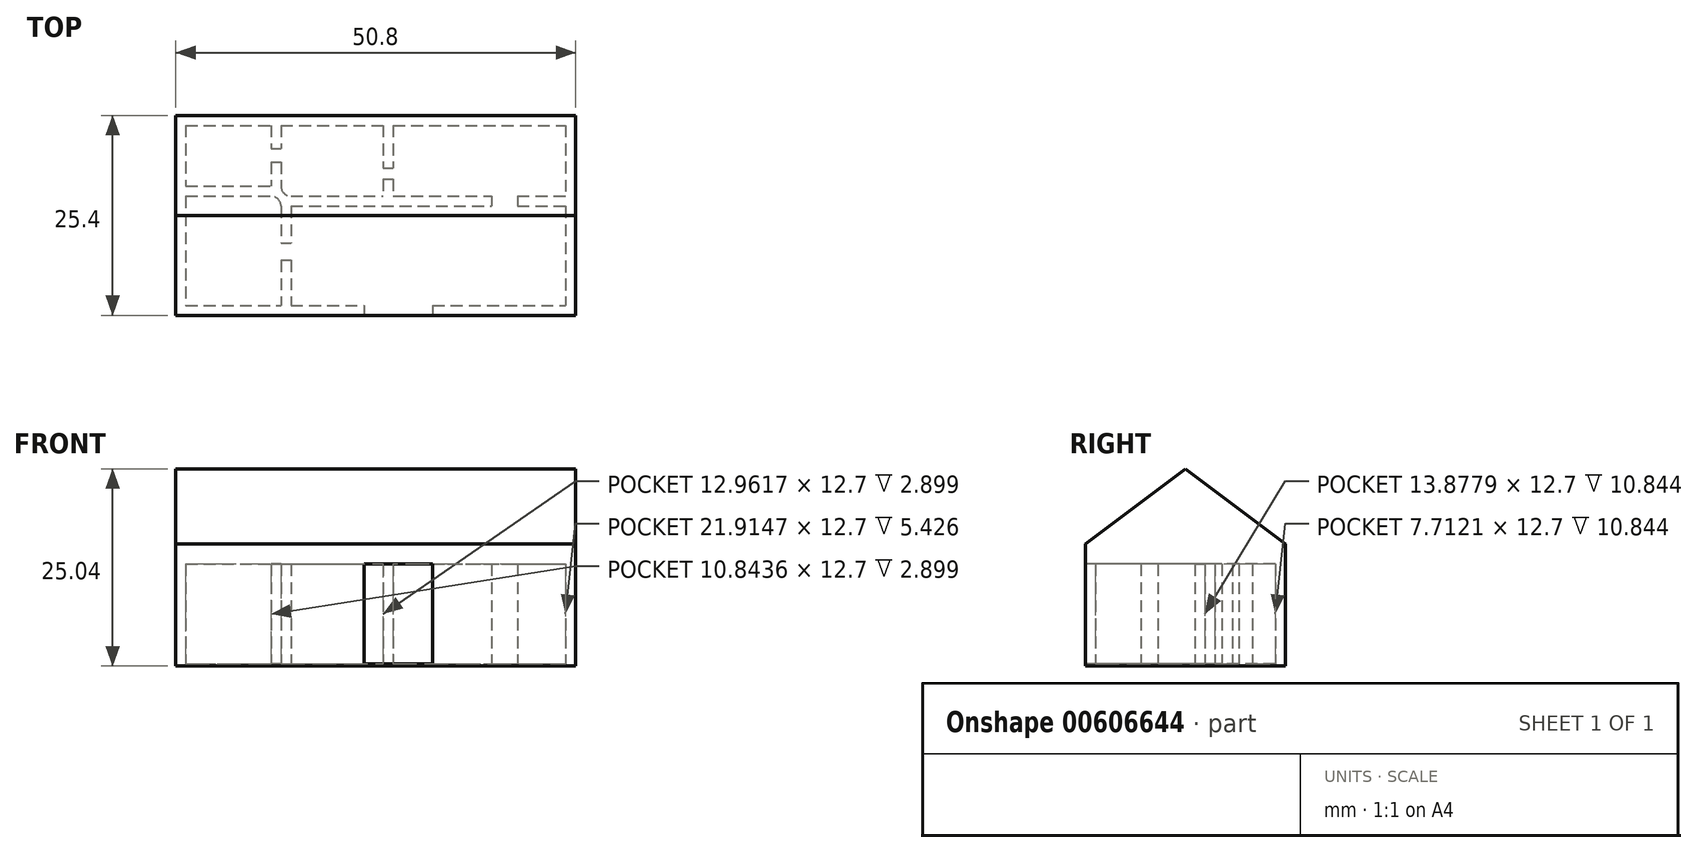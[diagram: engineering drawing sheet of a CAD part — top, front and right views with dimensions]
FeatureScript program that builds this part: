
annotation { "Feature Type Name" : "Feature", "Feature Type Description" : "" }
export const myFeature = defineFeature(function(context is Context, id is Id, definition is map)
    precondition{}
    {
        {
            var Q0;
            Q0=qCreatedBy(makeId("Top.planeOp"),FACE);
            var sketch = newSketch(context, id + "F0", { "sketchPlane" : qUnion([Q0])});
            skLineSegment(sketch, "E0.bottom", {"start": v(-23.3, 5.4) * mm, "end": v(27.5, 5.4) * mm});
            skLineSegment(sketch, "E0.top", {"start": v(-23.3, -20) * mm, "end": v(0.6, -20) * mm});
            skLineSegment(sketch, "E0.left", {"start": v(-23.3, 5.4) * mm, "end": v(-23.3, -20) * mm});
            skLineSegment(sketch, "E0.right", {"start": v(27.5, 5.4) * mm, "end": v(27.5, -20) * mm});
            skLineSegment(sketch, "E1.0", {"start": v(-22.03, 4.13) * mm, "end": v(3.04, 4.13) * mm});
            skLineSegment(sketch, "E1.1", {"start": v(-22.03, 4.13) * mm, "end": v(-22.03, -18.73) * mm});
            skLineSegment(sketch, "E1.2", {"start": v(-22.03, -18.73) * mm, "end": v(0.6, -18.73) * mm});
            skLineSegment(sketch, "E1.3", {"start": v(26.23, 4.13) * mm, "end": v(26.23, -18.73) * mm});
            skLineSegment(sketch, "E2", {"start": v(0.6, -18.73) * mm, "end": v(0.6, -20) * mm});
            skLineSegment(sketch, "E3", {"start": v(9.35, -18.73) * mm, "end": v(9.35, -20) * mm});
            skLineSegment(sketch, "E4.trimOffspring", {"start": v(9.35, -18.73) * mm, "end": v(26.23, -18.73) * mm});
            skLineSegment(sketch, "E5.trimOffspring", {"start": v(9.35, -20) * mm, "end": v(27.5, -20) * mm});
            skLineSegment(sketch, "E6.bottom", {"start": v(-22.03, 4.13) * mm, "end": v(-9.92, 4.13) * mm});
            skLineSegment(sketch, "E6.top", {"start": v(-22.03, -4.85) * mm, "end": v(-11.2, -4.85) * mm});
            skLineSegment(sketch, "E6.left", {"start": v(-22.03, 4.13) * mm, "end": v(-22.03, -4.85) * mm});
            skLineSegment(sketch, "E6.right", {"start": v(-9.92, 4.13) * mm, "end": v(-9.92, 1.23) * mm});
            skLineSegment(sketch, "E7.bottom", {"start": v(-8.65, -4.85) * mm, "end": v(3.04, -4.85) * mm});
            skLineSegment(sketch, "E7.top", {"start": v(-9.92, -18.73) * mm, "end": v(0.6, -18.73) * mm});
            skLineSegment(sketch, "E7.left", {"start": v(-9.92, -6.12) * mm, "end": v(-9.92, -10.78) * mm});
            skLineSegment(sketch, "E7.right", {"start": v(26.23, -4.85) * mm, "end": v(26.23, -18.73) * mm});
            skLineSegment(sketch, "E8.0", {"start": v(-22.03, -3.58) * mm, "end": v(-11.2, -3.58) * mm});
            skLineSegment(sketch, "E8.1", {"start": v(-11.2, 4.13) * mm, "end": v(-11.2, 1.23) * mm});
            skLineSegment(sketch, "E9.0", {"start": v(-8.65, -6.12) * mm, "end": v(16.82, -6.12) * mm});
            skLineSegment(sketch, "E9.1", {"start": v(-8.65, -6.12) * mm, "end": v(-8.65, -10.78) * mm});
            skArc(sketch, "E10", {"start": v(-9.92, -6.12) * mm, "mid": v(-10.3, -5.23) * mm, "end": v(-11.2, -4.85) * mm});
            skArc(sketch, "E11", {"start": v(-9.92, -3.58) * mm, "mid": v(-9.55, -4.48) * mm, "end": v(-8.65, -4.85) * mm});
            skLineSegment(sketch, "E12", {"start": v(-11.2, 1.23) * mm, "end": v(-9.92, 1.23) * mm});
            skLineSegment(sketch, "E13", {"start": v(-11.2, -0.52) * mm, "end": v(-9.92, -0.52) * mm});
            skLineSegment(sketch, "E14", {"start": v(-9.92, -10.78) * mm, "end": v(-8.65, -10.78) * mm});
            skPoint(sketch, "E14.endSnap0", {"position": v(-8.65, -12.43) * mm});
            skLineSegment(sketch, "E15", {"start": v(-9.92, -12.98) * mm, "end": v(-8.65, -12.98) * mm});
            skLineSegment(sketch, "E16", {"start": v(16.82, -4.85) * mm, "end": v(16.82, -6.12) * mm});
            skLineSegment(sketch, "E17", {"start": v(20.12, -4.85) * mm, "end": v(20.12, -6.12) * mm});
            skLineSegment(sketch, "E18.trimOffspring", {"start": v(-11.2, -0.52) * mm, "end": v(-11.2, -3.58) * mm});
            skLineSegment(sketch, "E19.trimOffspring", {"start": v(-9.92, -0.52) * mm, "end": v(-9.92, -3.58) * mm});
            skLineSegment(sketch, "E20.trimOffspring", {"start": v(-9.92, -12.98) * mm, "end": v(-9.92, -18.73) * mm});
            skLineSegment(sketch, "E21.trimOffspring", {"start": v(-8.65, -12.43) * mm, "end": v(-8.65, -18.73) * mm});
            skLineSegment(sketch, "E22.trimOffspring", {"start": v(20.12, -6.12) * mm, "end": v(26.23, -6.12) * mm});
            skLineSegment(sketch, "E23.trimOffspring", {"start": v(20.12, -4.85) * mm, "end": v(26.23, -4.85) * mm});
            skLineSegment(sketch, "E24", {"start": v(4.31, 4.13) * mm, "end": v(4.31, -1.3) * mm});
            skLineSegment(sketch, "E25.0", {"start": v(3.04, 4.13) * mm, "end": v(3.04, -1.3) * mm});
            skLineSegment(sketch, "E26", {"start": v(3.04, -1.3) * mm, "end": v(4.31, -1.3) * mm});
            skLineSegment(sketch, "E27", {"start": v(3.04, -2.67) * mm, "end": v(4.31, -2.67) * mm});
            skLineSegment(sketch, "E28.trimOffspring", {"start": v(3.04, -2.67) * mm, "end": v(3.04, -4.85) * mm});
            skLineSegment(sketch, "E29.trimOffspring", {"start": v(4.31, -2.67) * mm, "end": v(4.31, -4.85) * mm});
            skLineSegment(sketch, "E30.trimOffspring", {"start": v(4.31, -4.85) * mm, "end": v(16.82, -4.85) * mm});
            skLineSegment(sketch, "E31.trimOffspring", {"start": v(4.31, 4.13) * mm, "end": v(26.23, 4.13) * mm});
            skSolve(sketch);
        }
        {
            var Q0;
            Q0 = qSketchRegion(id + "F0", true);
            extrude(context, id + "F1", {"entities" : qUnion([Q0]), "depth" : 12.7 * mm, "offsetDistance" : 25.4 * mm});
        }
        {
            var Q0;
            Q0=makeQuery(id+"F1.opExtrude","CAP_FACE",FACE,{"disambiguationData":[OSD([sQuery(id+"F0.wireOp",EDGE,"E0.bottom"),sQuery(id+"F0.wireOp",EDGE,"E0.top"),sQuery(id+"F0.wireOp",EDGE,"E0.left"),sQuery(id+"F0.wireOp",EDGE,"E0.right"),sQuery(id+"F0.wireOp",EDGE,"E1.0"),sQuery(id+"F0.wireOp",EDGE,"E1.1"),sQuery(id+"F0.wireOp",EDGE,"E1.2"),sQuery(id+"F0.wireOp",EDGE,"E1.3"),sQuery(id+"F0.wireOp",EDGE,"E2"),sQuery(id+"F0.wireOp",EDGE,"E3"),sQuery(id+"F0.wireOp",EDGE,"E5.trimOffspring"),sQuery(id+"F0.wireOp",EDGE,"E6.bottom"),sQuery(id+"F0.wireOp",EDGE,"E6.top"),sQuery(id+"F0.wireOp",EDGE,"E6.left"),sQuery(id+"F0.wireOp",EDGE,"E6.right"),sQuery(id+"F0.wireOp",EDGE,"E7.bottom"),sQuery(id+"F0.wireOp",EDGE,"E7.top"),sQuery(id+"F0.wireOp",EDGE,"E7.left"),sQuery(id+"F0.wireOp",EDGE,"E7.right"),sQuery(id+"F0.wireOp",EDGE,"E8.0"),sQuery(id+"F0.wireOp",EDGE,"E8.1"),sQuery(id+"F0.wireOp",EDGE,"E9.0"),sQuery(id+"F0.wireOp",EDGE,"E9.1"),sQuery(id+"F0.wireOp",EDGE,"E10"),sQuery(id+"F0.wireOp",EDGE,"E11"),sQuery(id+"F0.wireOp",EDGE,"E12"),sQuery(id+"F0.wireOp",EDGE,"E13"),sQuery(id+"F0.wireOp",EDGE,"E14"),sQuery(id+"F0.wireOp",EDGE,"E15"),sQuery(id+"F0.wireOp",EDGE,"E16"),sQuery(id+"F0.wireOp",EDGE,"E17"),sQuery(id+"F0.wireOp",EDGE,"E18.trimOffspring"),sQuery(id+"F0.wireOp",EDGE,"E19.trimOffspring"),sQuery(id+"F0.wireOp",EDGE,"E20.trimOffspring"),sQuery(id+"F0.wireOp",EDGE,"E21.trimOffspring"),sQuery(id+"F0.wireOp",EDGE,"E4.trimOffspring"),sQuery(id+"F0.wireOp",EDGE,"E22.trimOffspring"),sQuery(id+"F0.wireOp",EDGE,"E23.trimOffspring"),sQuery(id+"F0.wireOp",EDGE,"E24"),sQuery(id+"F0.wireOp",EDGE,"E25.0"),sQuery(id+"F0.wireOp",EDGE,"E26"),sQuery(id+"F0.wireOp",EDGE,"E27"),sQuery(id+"F0.wireOp",EDGE,"E28.trimOffspring"),sQuery(id+"F0.wireOp",EDGE,"E29.trimOffspring"),sQuery(id+"F0.wireOp",EDGE,"E30.trimOffspring"),sQuery(id+"F0.wireOp",EDGE,"E31.trimOffspring")])],"isStart":false});
            var sketch = newSketch(context, id + "F2", { "sketchPlane" : qUnion([Q0])});
            skLineSegment(sketch, "E32.bottom", {"start": v(-23.3, 5.4) * mm, "end": v(27.5, 5.4) * mm});
            skLineSegment(sketch, "E32.top", {"start": v(-23.3, -20) * mm, "end": v(27.5, -20) * mm});
            skLineSegment(sketch, "E32.left", {"start": v(-23.3, 5.4) * mm, "end": v(-23.3, -20) * mm});
            skLineSegment(sketch, "E32.right", {"start": v(27.5, 5.4) * mm, "end": v(27.5, -20) * mm});
            skSolve(sketch);
        }
        {
            var Q0;
            Q0 = qSketchRegion(id + "F2", true);
            extrude(context, id + "F3", {"entities" : qUnion([Q0]), "operationType" : NewBodyOperationType.ADD, "depth" : 2.54 * mm, "offsetDistance" : 25.4 * mm});
        }
        {
            var Q0;
            Q0=makeQuery(id+"F3.boolean.opBoolean","MERGE",FACE,{"derivedFrom":[makeQuery(id+"F1.opExtrude","SWEPT_FACE",FACE,{"disambiguationData":[OSD([sQuery(id+"F0.wireOp",EDGE,"E0.left")])]}),makeQuery(id+"F3.opExtrude","SWEPT_FACE",FACE,{"disambiguationData":[OSD([sQuery(id+"F2.wireOp",EDGE,"E32.left")])]})]});
            var sketch = newSketch(context, id + "F4", { "sketchPlane" : qUnion([Q0])});
            skLineSegment(sketch, "E33", {"start": v(-5.4, 15.24) * mm, "end": v(7.3, 24.79) * mm});
            skPoint(sketch, "E33.endSnap0", {"position": v(7.3, 15.24) * mm});
            skLineSegment(sketch, "E34", {"start": v(7.3, 24.79) * mm, "end": v(20, 15.24) * mm});
            skLineSegment(sketch, "E35", {"start": v(-5.4, 15.24) * mm, "end": v(20, 15.24) * mm});
            skSolve(sketch);
        }
        {
            var Q0;
            Q0 = qSketchRegion(id + "F4", true);
            extrude(context, id + "F5", {"entities" : qUnion([Q0]), "operationType" : NewBodyOperationType.ADD, "oppositeDirection" : true, "depth" : 50.8 * mm, "offsetDistance" : 25.4 * mm});
        }
        {
            var Q0;
            Q0=makeQuery(id+"F1.opExtrude","CAP_FACE",FACE,{"disambiguationData":[OSD([sQuery(id+"F0.wireOp",EDGE,"E0.bottom"),sQuery(id+"F0.wireOp",EDGE,"E0.top"),sQuery(id+"F0.wireOp",EDGE,"E0.left"),sQuery(id+"F0.wireOp",EDGE,"E0.right"),sQuery(id+"F0.wireOp",EDGE,"E1.0"),sQuery(id+"F0.wireOp",EDGE,"E1.1"),sQuery(id+"F0.wireOp",EDGE,"E1.2"),sQuery(id+"F0.wireOp",EDGE,"E1.3"),sQuery(id+"F0.wireOp",EDGE,"E2"),sQuery(id+"F0.wireOp",EDGE,"E3"),sQuery(id+"F0.wireOp",EDGE,"E5.trimOffspring"),sQuery(id+"F0.wireOp",EDGE,"E6.bottom"),sQuery(id+"F0.wireOp",EDGE,"E6.top"),sQuery(id+"F0.wireOp",EDGE,"E6.left"),sQuery(id+"F0.wireOp",EDGE,"E6.right"),sQuery(id+"F0.wireOp",EDGE,"E7.bottom"),sQuery(id+"F0.wireOp",EDGE,"E7.top"),sQuery(id+"F0.wireOp",EDGE,"E7.left"),sQuery(id+"F0.wireOp",EDGE,"E7.right"),sQuery(id+"F0.wireOp",EDGE,"E8.0"),sQuery(id+"F0.wireOp",EDGE,"E8.1"),sQuery(id+"F0.wireOp",EDGE,"E9.0"),sQuery(id+"F0.wireOp",EDGE,"E9.1"),sQuery(id+"F0.wireOp",EDGE,"E10"),sQuery(id+"F0.wireOp",EDGE,"E11"),sQuery(id+"F0.wireOp",EDGE,"E12"),sQuery(id+"F0.wireOp",EDGE,"E13"),sQuery(id+"F0.wireOp",EDGE,"E14"),sQuery(id+"F0.wireOp",EDGE,"E15"),sQuery(id+"F0.wireOp",EDGE,"E16"),sQuery(id+"F0.wireOp",EDGE,"E17"),sQuery(id+"F0.wireOp",EDGE,"E18.trimOffspring"),sQuery(id+"F0.wireOp",EDGE,"E19.trimOffspring"),sQuery(id+"F0.wireOp",EDGE,"E20.trimOffspring"),sQuery(id+"F0.wireOp",EDGE,"E21.trimOffspring"),sQuery(id+"F0.wireOp",EDGE,"E4.trimOffspring"),sQuery(id+"F0.wireOp",EDGE,"E22.trimOffspring"),sQuery(id+"F0.wireOp",EDGE,"E23.trimOffspring"),sQuery(id+"F0.wireOp",EDGE,"E24"),sQuery(id+"F0.wireOp",EDGE,"E25.0"),sQuery(id+"F0.wireOp",EDGE,"E26"),sQuery(id+"F0.wireOp",EDGE,"E27"),sQuery(id+"F0.wireOp",EDGE,"E28.trimOffspring"),sQuery(id+"F0.wireOp",EDGE,"E29.trimOffspring"),sQuery(id+"F0.wireOp",EDGE,"E30.trimOffspring"),sQuery(id+"F0.wireOp",EDGE,"E31.trimOffspring")])],"isStart":true});
            var sketch = newSketch(context, id + "F6", { "sketchPlane" : qUnion([Q0])});
            skLineSegment(sketch, "E36.bottom", {"start": v(-23.3, 20) * mm, "end": v(27.5, 20) * mm});
            skLineSegment(sketch, "E36.top", {"start": v(-23.3, -5.4) * mm, "end": v(27.5, -5.4) * mm});
            skLineSegment(sketch, "E36.left", {"start": v(-23.3, 20) * mm, "end": v(-23.3, -5.4) * mm});
            skLineSegment(sketch, "E36.right", {"start": v(27.5, 20) * mm, "end": v(27.5, -5.4) * mm});
            skSolve(sketch);
        }
        {
            var Q0;
            Q0 = qSketchRegion(id + "F6", true);
            extrude(context, id + "F7", {"entities" : qUnion([Q0]), "operationType" : NewBodyOperationType.ADD, "depth" : 0.25 * mm, "offsetDistance" : 25.4 * mm});
        }
    });
